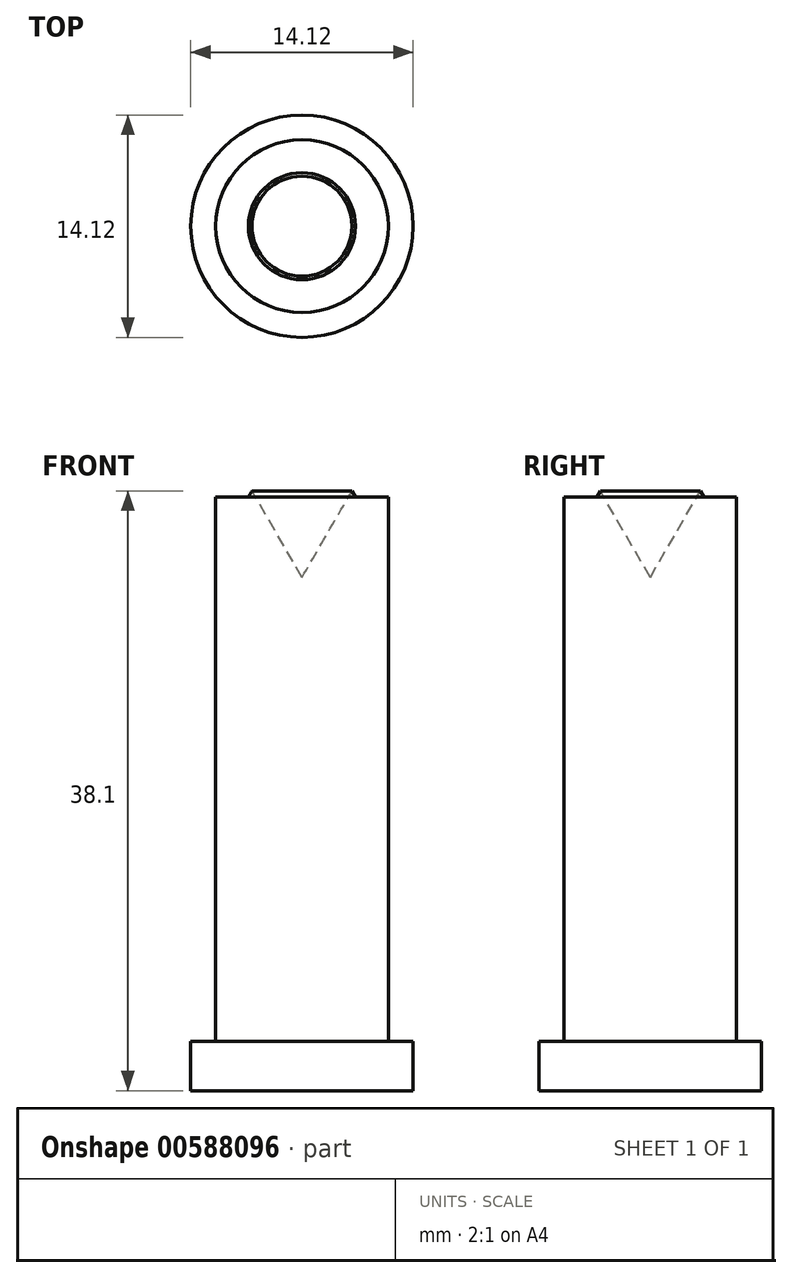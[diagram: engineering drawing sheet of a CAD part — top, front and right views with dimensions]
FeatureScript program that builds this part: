
annotation { "Feature Type Name" : "Feature", "Feature Type Description" : "" }
export const myFeature = defineFeature(function(context is Context, id is Id, definition is map)
    precondition{}
    {
        {
            var Q0;
            Q0=qCreatedBy(makeId("Front.planeOp"),FACE);
            var sketch = newSketch(context, id + "F0", { "sketchPlane" : qUnion([Q0])});
            skLineSegment(sketch, "E0", {"start": v(0, 0) * mm, "end": v(7.06, 0) * mm});
            skLineSegment(sketch, "E1", {"start": v(7.06, 0) * mm, "end": v(7.06, 3.12) * mm});
            skLineSegment(sketch, "E2", {"start": v(7.06, 3.12) * mm, "end": v(5.49, 3.12) * mm});
            skLineSegment(sketch, "E3", {"start": v(5.49, 3.12) * mm, "end": v(5.49, 37.72) * mm});
            skLineSegment(sketch, "E4", {"start": v(5.49, 37.72) * mm, "end": v(3.4, 37.72) * mm});
            skLineSegment(sketch, "E5", {"start": v(0, 0) * mm, "end": v(0, 32.6) * mm});
            skLineSegment(sketch, "E6", {"start": v(3.18, 38.1) * mm, "end": v(3.4, 37.72) * mm});
            skLineSegment(sketch, "E7", {"start": v(3.17, 38.1) * mm, "end": v(0, 32.6) * mm});
            skSolve(sketch);
        }
        {
            var Q0;
            Q0 = qSketchRegion(id + "F0", true);
            var Q1;
            Q1=sQuery(id+"F0.wireOp",EDGE,"E5");
            revolve(context, id + "F1", {"entities" : qUnion([Q0]), "axis" : qUnion([Q1]), "revolveType" : RevolveType.FULL});
        }
    });
